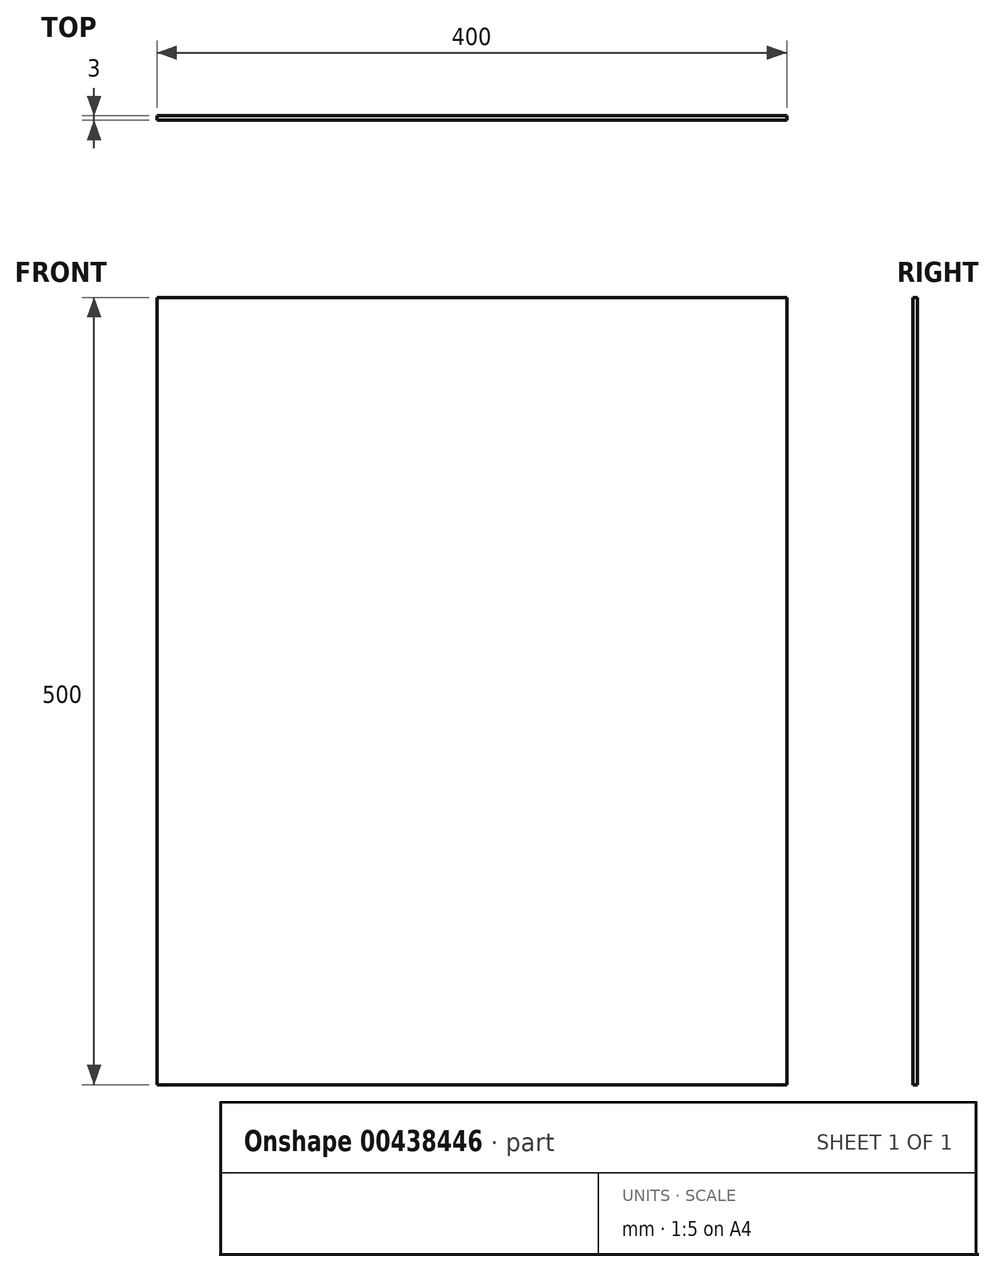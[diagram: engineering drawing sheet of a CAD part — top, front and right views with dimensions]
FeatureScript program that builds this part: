
annotation { "Feature Type Name" : "Feature", "Feature Type Description" : "" }
export const myFeature = defineFeature(function(context is Context, id is Id, definition is map)
    precondition{}
    {
        {
            var Q0;
            Q0=qCreatedBy(makeId("Front.planeOp"),FACE);
            var sketch = newSketch(context, id + "F0", { "sketchPlane" : qUnion([Q0])});
            skLineSegment(sketch, "E0.bottom", {"start": v(-200, 500) * mm, "end": v(200, 500) * mm});
            skLineSegment(sketch, "E0.top", {"start": v(-200, 0) * mm, "end": v(200, 0) * mm});
            skLineSegment(sketch, "E0.left", {"start": v(-200, 500) * mm, "end": v(-200, 0) * mm});
            skLineSegment(sketch, "E0.right", {"start": v(200, 500) * mm, "end": v(200, 0) * mm});
            skSolve(sketch);
        }
        {
            var Q0;
            Q0=makeQuery(id+"F0.imprint","IMPRINT",FACE,{"disambiguationData":[TD([[makeQuery(id+"F0.imprint","IMPRINT",EDGE,{"derivedFrom":sQuery(id+"F0.wireOp",EDGE,"E0.bottom")}),-1.0]])]});
            extrude(context, id + "F1", {"entities" : qUnion([Q0]), "oppositeDirection" : true, "depth" : 3 * mm});
        }
    });
